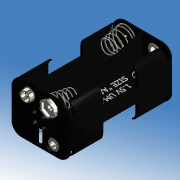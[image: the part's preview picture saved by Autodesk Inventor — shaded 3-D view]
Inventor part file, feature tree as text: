
AUTODESK INVENTOR PART (.ipt)
format: ipt  version: 2015 (Build 190159000, 159)  size: 1,797,632 bytes
history: native  units: mm (DEFAULTED — no unit token found)
features: other x13, sketch x3
ambient origin geometry x8: Origin, YZ Plane, XZ Plane, XY Plane, X Axis, Y Axis, Z Axis, Center Point
bodies: Solid1 (feature_tree)
feature tree (16):
  other  "23T0526-001 ASSY.iam"
  other  "23T0526-001 BODY.ipt:1"
  other  "23T0526-001 SPRING 1.ipt:1"
  other  "23T0526-001 SPRING 1.ipt:2"
  other  "23T0526-001 SPRING 1.ipt:3"
  other  "23T0526-001 SPRING 2.ipt:1"
  other  "23T0526-001 RIVET 1.ipt:1"
  other  "23T0526-001 RIVET 1.ipt:2"
  other  "23T0526-001 RIVET 1.ipt:3"
  other  "23T0526-001 CONT-HEX.ipt:1"
  other  "23T0526-001 CONT-ROUND.ipt:1"
  other  "23T0526-001 RIVET 2.ipt:1"
  other  "23T0526-001 RIVET 3.ipt:1"
  sketch  "Sketch3"
  sketch  "Sketch3_1"  dims[d0=10.0mm]
  sketch  "Sketch3_2"
